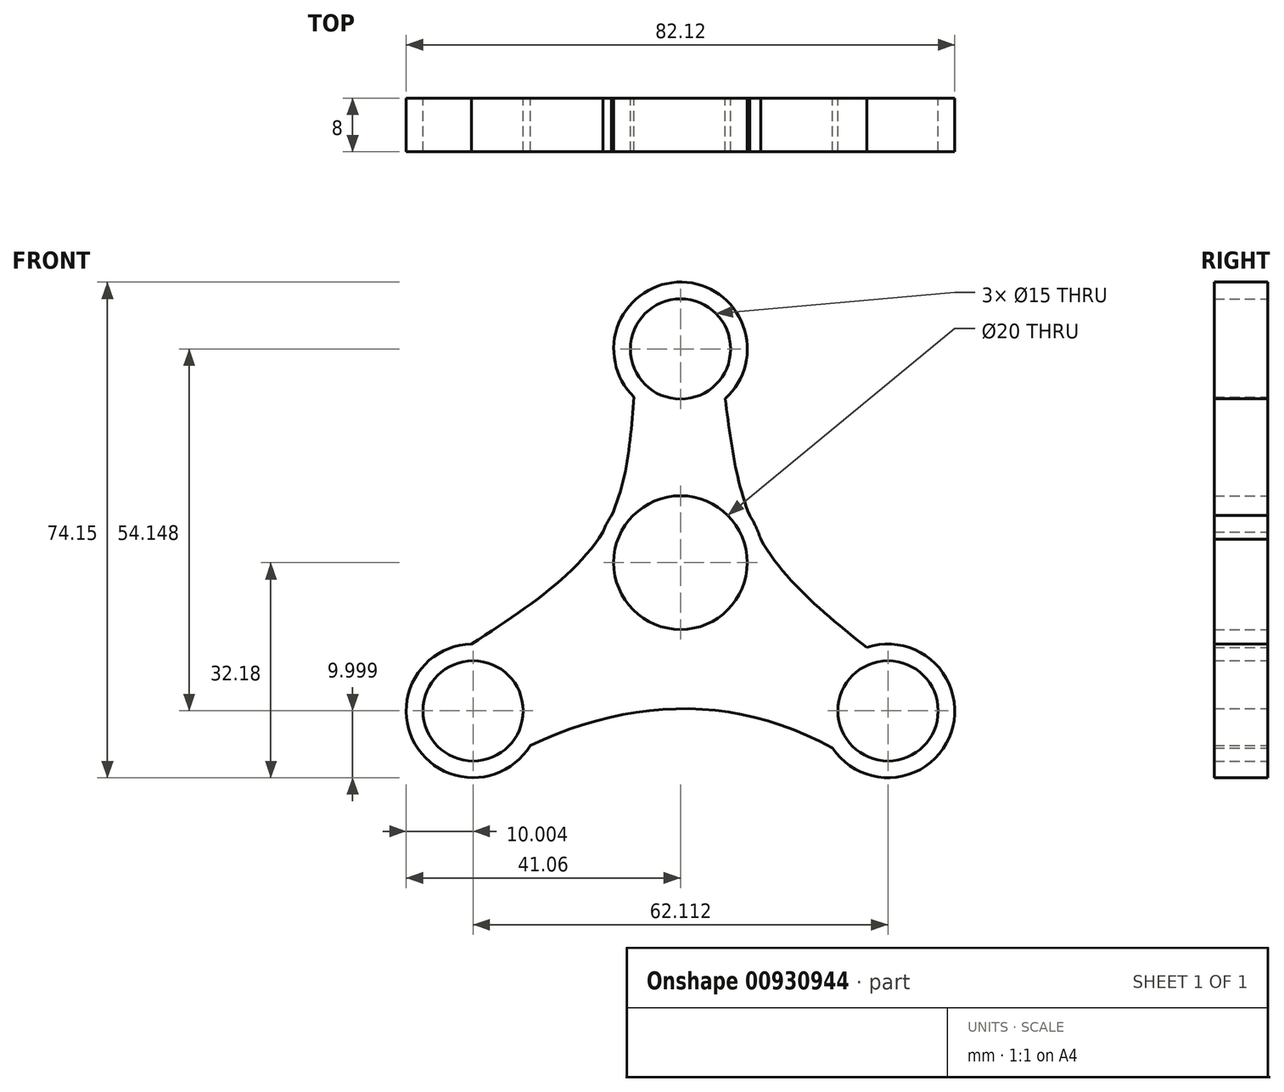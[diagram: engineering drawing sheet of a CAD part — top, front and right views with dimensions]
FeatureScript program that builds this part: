
annotation { "Feature Type Name" : "Feature", "Feature Type Description" : "" }
export const myFeature = defineFeature(function(context is Context, id is Id, definition is map)
    precondition{}
    {
        {
            var Q0;
            Q0=qCreatedBy(makeId("Front.planeOp"),FACE);
            var sketch = newSketch(context, id + "F0", { "sketchPlane" : qUnion([Q0])});
            skCircle(sketch, "E0", {"center": v(31.06, -22.18) * mm, "radius": 10 * mm});
            skCircle(sketch, "E1", {"center": v(31.06, -22.18) * mm, "radius": 7.5 * mm});
            skCircle(sketch, "E2.MirrorC", {"center": v(-31.06, -22.18) * mm, "radius": 7.5 * mm});
            skCircle(sketch, "E3.MirrorC", {"center": v(-31.06, -22.18) * mm, "radius": 10 * mm});
            skCircle(sketch, "E4", {"center": v(0, 0) * mm, "radius": 10 * mm});
            skCircle(sketch, "E5", {"center": v(0, 0) * mm, "radius": 12.5 * mm});
            skCircle(sketch, "E6", {"center": v(0, 31.97) * mm, "radius": 7.5 * mm});
            skCircle(sketch, "E7", {"center": v(0, 31.97) * mm, "radius": 10 * mm});
            skFitSpline(sketch, "E8", {"points": [v(-6.96, 24.8) * mm, v(-11.63, 4.57) * mm, v(-31.3, -12.18) * mm], "startDerivative": vector(-3.57, -45.3) * mm, "endDerivative": vector(-44.36, -28.96) * mm});
            skFitSpline(sketch, "E9", {"points": [v(6.69, 24.53) * mm, v(12, 3.5) * mm, v(27.86, -12.7) * mm], "startDerivative": vector(5.83, -45.06) * mm, "endDerivative": vector(36.41, -29.46) * mm});
            skFitSpline(sketch, "E10", {"points": [v(-22.5, -27.35) * mm, v(22.74, -27.74) * mm], "startDerivative": vector(45.44, 21.35) * mm, "endDerivative": vector(44, -24.16) * mm});
            skSolve(sketch);
        }
        {
            var Q0;
            Q0 = qSketchRegion(id + "F0", true);
            extrude(context, id + "F1", {"entities" : qUnion([Q0]), "depth" : 8 * mm, "offsetDistance" : 25 * mm});
        }
    });
